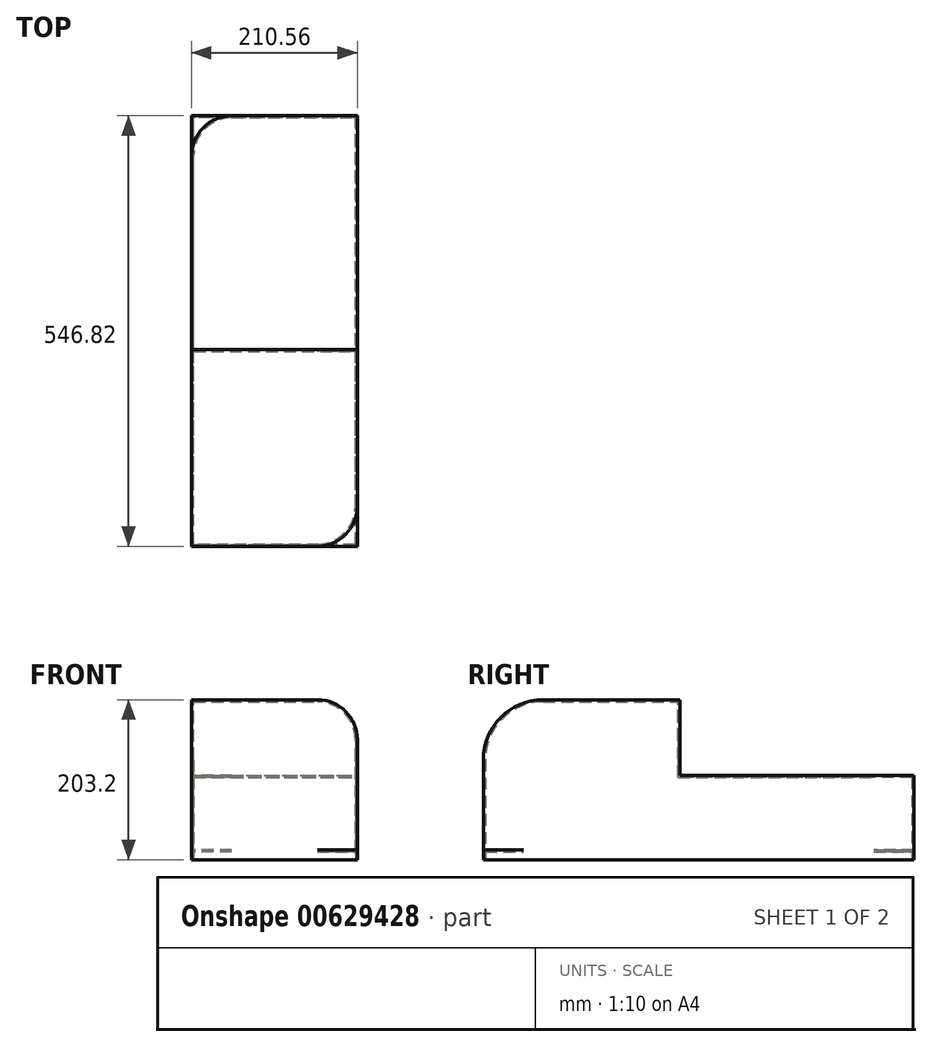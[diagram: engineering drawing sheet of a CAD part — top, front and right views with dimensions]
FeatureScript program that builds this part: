
annotation { "Feature Type Name" : "Feature", "Feature Type Description" : "" }
export const myFeature = defineFeature(function(context is Context, id is Id, definition is map)
    precondition{}
    {
        {
            var Q0;
            Q0=qCreatedBy(makeId("Top.planeOp"),FACE);
            var sketch = newSketch(context, id + "F0", { "sketchPlane" : qUnion([Q0])});
            skLineSegment(sketch, "E0.bottom", {"start": v(105.28, -273.4) * mm, "end": v(-105.28, -273.4) * mm});
            skLineSegment(sketch, "E0.top", {"start": v(105.28, 273.4) * mm, "end": v(-105.28, 273.4) * mm});
            skLineSegment(sketch, "E0.left", {"start": v(105.28, -273.4) * mm, "end": v(105.28, 273.4) * mm});
            skLineSegment(sketch, "E0.right", {"start": v(-105.28, -273.4) * mm, "end": v(-105.28, 273.4) * mm});
            skPoint(sketch, "E0.middle", {"position": v(0, 0) * mm});
            skSolve(sketch);
        }
        {
            var Q0;
            Q0=makeQuery(id+"F0.imprint","IMPRINT",FACE,{"disambiguationData":[TD([[makeQuery(id+"F0.imprint","IMPRINT",EDGE,{"derivedFrom":sQuery(id+"F0.wireOp",EDGE,"E0.bottom")}),-1.0]])]});
            extrude(context, id + "F1", {"entities" : qUnion([Q0]), "depth" : 203.2 * mm, "offsetDistance" : 25.4 * mm});
        }
        {
            var Q0;
            Q0=makeQuery(id+"F1.opExtrude","SWEPT_FACE",FACE,{"disambiguationData":[OSD([sQuery(id+"F0.wireOp",EDGE,"E0.left")])]});
            var sketch = newSketch(context, id + "F2", { "sketchPlane" : qUnion([Q0])});
            skLineSegment(sketch, "E1.bottom", {"start": v(273.4, 203.2) * mm, "end": v(-23.58, 203.2) * mm});
            skLineSegment(sketch, "E1.top", {"start": v(273.4, 107.33) * mm, "end": v(-23.58, 107.33) * mm});
            skLineSegment(sketch, "E1.left", {"start": v(273.4, 203.2) * mm, "end": v(273.4, 107.33) * mm});
            skLineSegment(sketch, "E1.right", {"start": v(-23.58, 203.2) * mm, "end": v(-23.58, 107.33) * mm});
            skSolve(sketch);
        }
        {
            var Q0;
            Q0=makeQuery(id+"F2.imprint","IMPRINT",FACE,{"disambiguationData":[TD([[makeQuery(id+"F2.imprint","IMPRINT",EDGE,{"derivedFrom":sQuery(id+"F2.wireOp",EDGE,"E1.bottom")}),-1.0]])]});
            extrude(context, id + "F3", {"entities" : qUnion([Q0]), "operationType" : NewBodyOperationType.REMOVE, "endBound" : BoundingType.THROUGH_ALL, "oppositeDirection" : true, "depth" : 25.4 * mm, "offsetDistance" : 25.4 * mm});
        }
        {
            var Q0;
            Q0=makeQuery(id+"F3.boolean.opBoolean","COPY",EDGE,{"derivedFrom":makeQuery(id+"F3.opExtrude","SWEPT_EDGE",EDGE,{"disambiguationData":[OSD([sQuery(id+"F0.wireOp",EDGE,"E0.left"),sQuery(id+"F2.wireOp",EDGE,"E1.bottom"),sQuery(id+"F2.wireOp",EDGE,"E1.right")])]})});
            var Q1;
            Q1=makeQuery(id+"F1.opExtrude","CAP_EDGE",EDGE,{"disambiguationData":[OSD([sQuery(id+"F0.wireOp",EDGE,"E0.bottom")])],"isStart":false});
            var Q2;
            Q2=makeQuery(id+"F3.boolean.opBoolean","COPY",EDGE,{"derivedFrom":makeQuery(id+"F3.opExtrude","SWEPT_EDGE",EDGE,{"disambiguationData":[OSD([sQuery(id+"F0.wireOp",EDGE,"E0.top"),sQuery(id+"F0.wireOp",EDGE,"E0.left"),sQuery(id+"F2.wireOp",EDGE,"E1.top"),sQuery(id+"F2.wireOp",EDGE,"E1.left")])]})});
            fillet(context, id + "F4", {"entities" : qUnion([Q0, Q1, Q2]), "radius" : 76.2 * mm, "tangentPropagation" : true, "allowEdgeOverflow" : false});
        }
        {
            var Q0;
            Q0=makeQuery(id+"F1.opExtrude","CAP_EDGE",EDGE,{"disambiguationData":[OSD([sQuery(id+"F0.wireOp",EDGE,"E0.left")])],"isStart":false});
            var Q1;
            Q1=makeQuery(id+"F3.boolean.opBoolean","COPY",EDGE,{"derivedFrom":makeQuery(id+"F3.opExtrude","CAP_EDGE",EDGE,{"disambiguationData":[OSD([sQuery(id+"F2.wireOp",EDGE,"E1.top")])],"isStart":true})});
            var Q2;
            Q2=makeQuery(id+"F1.opExtrude","SWEPT_EDGE",EDGE,{"disambiguationData":[OSD([sQuery(id+"F0.wireOp",EDGE,"E0.top"),sQuery(id+"F0.wireOp",EDGE,"E0.right")])]});
            var Q3;
            Q3=makeQuery(id+"F4.opFillet","BLEND_EDGE",EDGE,{"blendedFrom":[makeQuery(id+"F3.boolean.opBoolean","COPY",EDGE,{"derivedFrom":makeQuery(id+"F3.opExtrude","SWEPT_EDGE",EDGE,{"disambiguationData":[OSD([sQuery(id+"F0.wireOp",EDGE,"E0.left"),sQuery(id+"F2.wireOp",EDGE,"E1.bottom"),sQuery(id+"F2.wireOp",EDGE,"E1.right")])]})}),makeQuery(id+"F1.opExtrude","SWEPT_FACE",FACE,{"disambiguationData":[OSD([sQuery(id+"F0.wireOp",EDGE,"E0.right")])]})],"blendedInto":[makeQuery(id+"F1.opExtrude","SWEPT_FACE",FACE,{"disambiguationData":[OSD([sQuery(id+"F0.wireOp",EDGE,"E0.right")])]})]});
            fillet(context, id + "F5", {"entities" : qUnion([Q0, Q1, Q2, Q3]), "radius" : 50.8 * mm, "tangentPropagation" : true, "allowEdgeOverflow" : false});
        }
        {
            var Q0;
            Q0=makeQuery(id+"F0.imprint","IMPRINT",FACE,{"disambiguationData":[TD([[makeQuery(id+"F0.imprint","IMPRINT",EDGE,{"derivedFrom":sQuery(id+"F0.wireOp",EDGE,"E0.bottom")}),-1.0]])]});
            extrude(context, id + "F6", {"entities" : qUnion([Q0]), "operationType" : NewBodyOperationType.ADD, "depth" : 12.7 * mm, "offsetDistance" : 25.4 * mm});
        }
        {
            var Q0;
            {var subQ0=sQuery(id+"F0.wireOp",EDGE,"E0.right");var subQ1=sQuery(id+"F0.wireOp",EDGE,"E0.left");var subQ2=sQuery(id+"F0.wireOp",EDGE,"E0.top");var subQ3=sQuery(id+"F0.wireOp",EDGE,"E0.bottom");Q0=makeQuery(id+"F6.boolean.opBoolean","MERGE",FACE,{"derivedFrom":[makeQuery(id+"F1.opExtrude","CAP_FACE",FACE,{"disambiguationData":[OSD([subQ3,subQ2,subQ1,subQ0])],"isStart":true}),makeQuery(id+"F6.opExtrude","CAP_FACE",FACE,{"disambiguationData":[OSD([subQ3,subQ2,subQ1,subQ0])],"isStart":true})]});}
            shell(context, id + "F7", {"entities" : qUnion([Q0]), "thickness" : 2.54 * mm});
        }
    });
